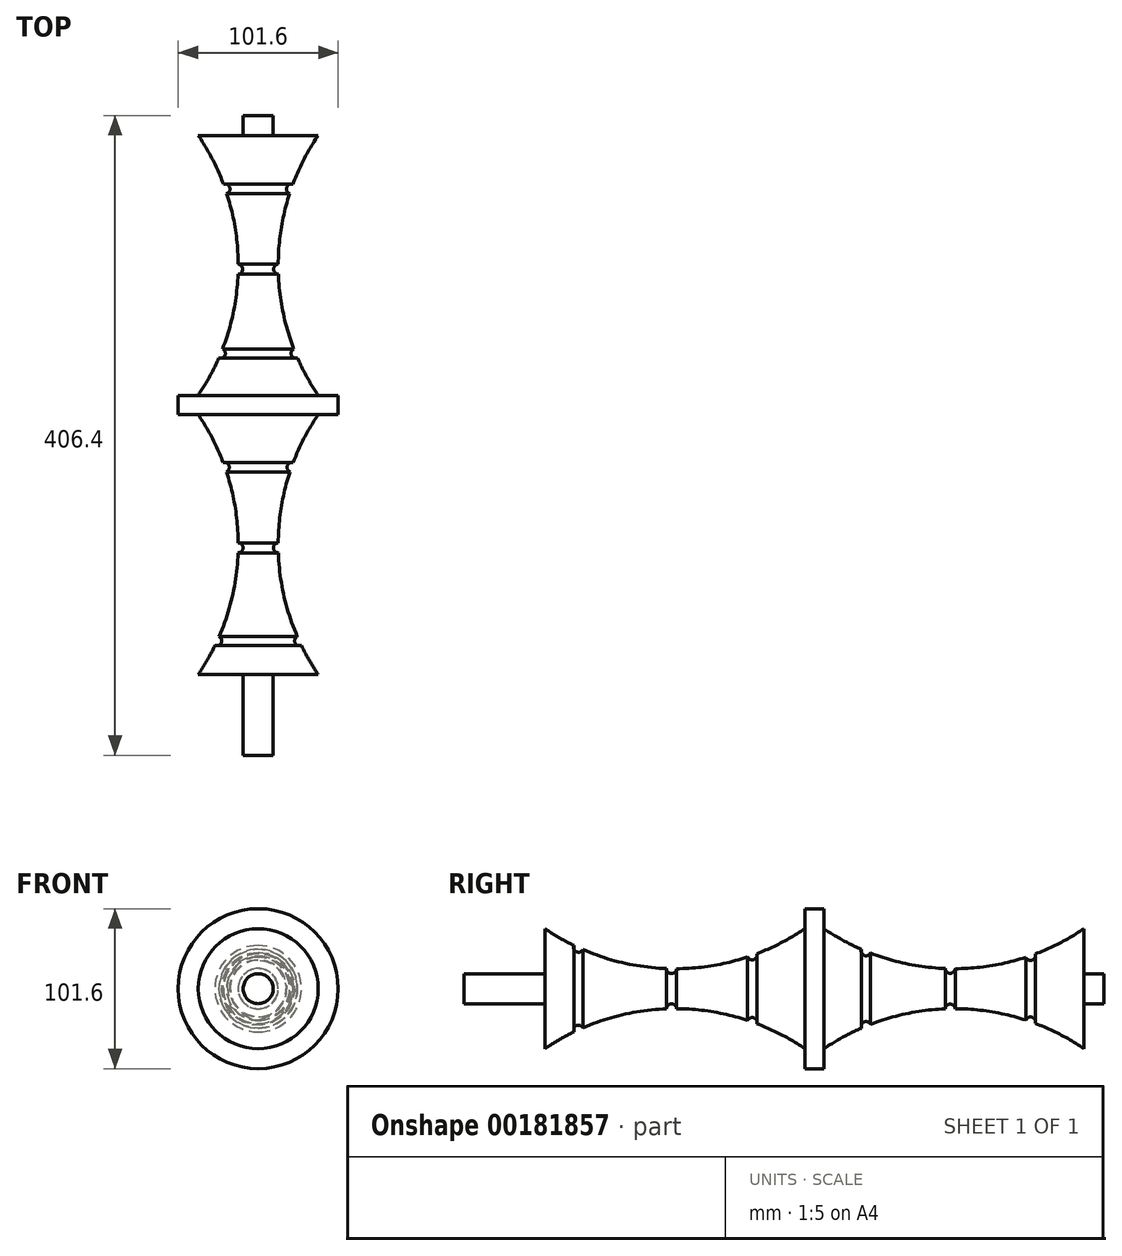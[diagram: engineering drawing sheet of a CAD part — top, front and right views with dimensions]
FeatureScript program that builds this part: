
annotation { "Feature Type Name" : "Feature", "Feature Type Description" : "" }
export const myFeature = defineFeature(function(context is Context, id is Id, definition is map)
    precondition{}
    {
        {
            var Q0;
            Q0=qCreatedBy(makeId("Front.planeOp"),FACE);
            var sketch = newSketch(context, id + "F0", { "sketchPlane" : qUnion([Q0])});
            skCircle(sketch, "E0", {"center": v(0, 0) * mm, "radius": 9.53 * mm});
            skSolve(sketch);
        }
        {
            var Q0;
            Q0 = qSketchRegion(id + "F0", true);
            extrude(context, id + "F1", {"entities" : qUnion([Q0]), "depth" : 406.4 * mm});
        }
        {
            var Q0;
            Q0=qCreatedBy(makeId("Right.planeOp"),FACE);
            var sketch = newSketch(context, id + "F2", { "sketchPlane" : qUnion([Q0])});
            skLineSegment(sketch, "E1", {"start": v(-12.7, 0) * mm, "end": v(-12.7, 38.1) * mm});
            skLineSegment(sketch, "E2", {"start": v(-177.8, 38.1) * mm, "end": v(-177.8, 50.8) * mm});
            skLineSegment(sketch, "E3", {"start": v(-177.8, 50.8) * mm, "end": v(-190, 50.8) * mm});
            skLineSegment(sketch, "E4", {"start": v(-190, 50.8) * mm, "end": v(-190, 38.1) * mm});
            skLineSegment(sketch, "E5", {"start": v(-355.1, 38.1) * mm, "end": v(-355.1, 0) * mm});
            skArc(sketch, "E6", {"start": v(-177.8, 38.1) * mm, "mid": v(-95.25, 12.7) * mm, "end": v(-12.7, 38.1) * mm});
            skArc(sketch, "E7", {"start": v(-355.1, 38.1) * mm, "mid": v(-272.54, 12.7) * mm, "end": v(-190, 38.1) * mm});
            skLineSegment(sketch, "E8", {"start": v(-12.7, 0) * mm, "end": v(-355.1, 0) * mm});
            skSolve(sketch);
        }
        {
            var Q0;
            Q0 = qSketchRegion(id + "F2", true);
            var Q1;
            Q1=sQuery(id+"F2.wireOp",EDGE,"E8");
            revolve(context, id + "F3", {"operationType" : NewBodyOperationType.ADD, "entities" : qUnion([Q0]), "axis" : qUnion([Q1]), "revolveType" : RevolveType.FULL});
        }
        {
            var Q0;
            Q0=qCreatedBy(makeId("Right.planeOp"),FACE);
            var sketch = newSketch(context, id + "F4", { "sketchPlane" : qUnion([Q0])});
            skCircle(sketch, "E9", {"center": v(-274.7, 12.8) * mm, "radius": 3.18 * mm});
            skCircle(sketch, "E10", {"center": v(-223.5, 21.5) * mm, "radius": 3.18 * mm});
            skCircle(sketch, "E11", {"center": v(-333.77, 26.34) * mm, "radius": 3.18 * mm});
            skCircle(sketch, "E12", {"center": v(-97.68, 12.95) * mm, "radius": 3.18 * mm});
            skCircle(sketch, "E13", {"center": v(-46.68, 21.1) * mm, "radius": 3.18 * mm});
            skCircle(sketch, "E14", {"center": v(-151.18, 24.03) * mm, "radius": 3.18 * mm});
            skSolve(sketch);
        }
        {
            var Q0;
            Q0 = qSketchRegion(id + "F4", true);
            var Q1;
            {var subQ0=sQuery(id+"F0.wireOp",EDGE,"E0");Q1=makeQuery(id+"F3.boolean.opBoolean","SPLIT",FACE,{"disambiguationData":[TD([makeQuery(id+"F1.opExtrude","CAP_FACE",FACE,{"disambiguationData":[OSD([subQ0])],"isStart":true})])],"derivedFrom":makeQuery(id+"F1.opExtrude","SWEPT_FACE",FACE,{"disambiguationData":[OSD([subQ0])]})});}
            revolve(context, id + "F5", {"operationType" : NewBodyOperationType.REMOVE, "entities" : qUnion([Q0]), "axis" : qUnion([Q1]), "revolveType" : RevolveType.FULL, "oppositeDirection" : true});
        }
    });
